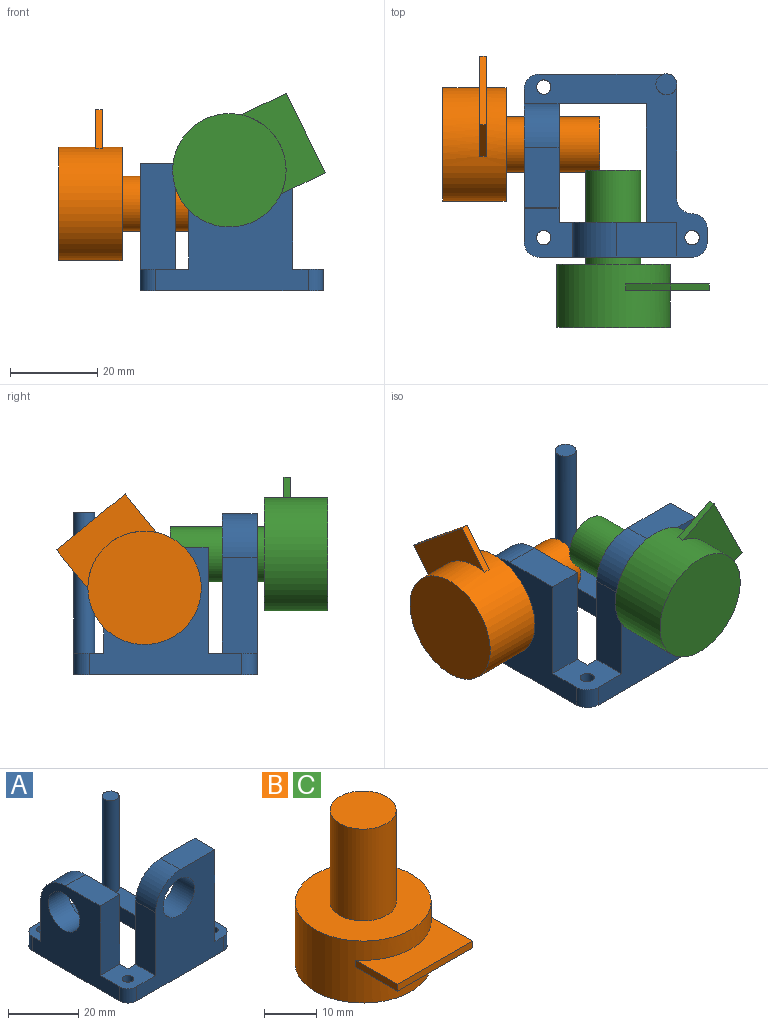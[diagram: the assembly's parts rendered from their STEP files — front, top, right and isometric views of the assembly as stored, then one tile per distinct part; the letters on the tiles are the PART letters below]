
ASSEMBLY  parts=3 mates=2
PART A: 32 faces, bbox 42x42x37.2 mm
  f0: plane 42x42mm, normal (0,0,1), area 458.1mm2, adj f3,f4,f5,f6,f7,f8,f9,f10
  f1: plane 11.25x11.1mm, normal (0,0,1), area 103.6mm2, adj f2,f5,f6,f11,f14,f18,f21,f26
  f2: plane 29.3x27.15mm, normal (1,0,0), area 568.4mm2, adj f1,f3,f11,f12,f20,f21,f22,f28
  f3: plane 20x5mm, normal (0,-1,0), area 100mm2, adj f0,f2,f4,f12
  f4: plane 27.15x5mm, normal (-1,0,0), area 135.7mm2, adj f0,f3,f11,f12
  f5: plane 35x29.3mm, normal (-1,0,0), area 607.6mm2, adj f0,f1,f12,f20,f21,f22,f23,f26
  f6: plane 37x35mm, normal (0,-1,0), area 791.7mm2, adj f0,f1,f12,f17,f18,f19,f24,f26
  f7: plane 5x3mm, normal (1,0,0), area 15mm2, adj f0,f12,f24,f25
  f8: plane 26.1x5mm, normal (1,0,0), area 130.5mm2, adj f0,f9,f12,f27
  f9: cylinder r=2.4mm len=37.2mm, axis (0,0,-1), area 504.4mm2, adj f0,f8,f10,f12,f16
  f10: plane 29.1x5mm, normal (0,1,0), area 145.5mm2, adj f0,f9,f12,f23
  f11: plane 37x27mm, normal (0,1,0), area 716.7mm2, adj f0,f1,f2,f4,f12,f17,f18,f19
  f12: plane 42x42mm, normal (0,0,-1), area 962.2mm2, adj f2,f3,f4,f5,f6,f7,f8,f9
  f13: cylinder r=1.65mm len=5mm, axis (0,0,-1), area 51.8mm2, adj f0,f12
  f14: cylinder r=1.65mm len=5mm, axis (0,0,-1), area 51.8mm2, adj f1,f12
  f15: cylinder r=1.65mm len=5mm, axis (0,0,-1), area 51.8mm2, adj f0,f12
  f16: plane 4.8x4.8mm, normal (0,0,1), area 18.1mm2, adj f9
  f17: plane 32x8mm, normal (1,0,0), area 256mm2, adj f0,f6,f11,f19
  f18: plane 22x8mm, normal (-1,0,0), area 176mm2, adj f1,f6,f11,f31
  f19: plane 13.9x8mm, normal (0,0,1), area 111.2mm2, adj f6,f11,f17,f31
  f20: plane 14.3x8mm, normal (0,1,0), area 114.4mm2, adj f0,f2,f5,f30
  f21: plane 24.3x8mm, normal (0,-1,0), area 194.4mm2, adj f1,f2,f5,f22
  f22: plane 13.9x8mm, normal (0,0,1), area 111.2mm2, adj f2,f5,f21,f30
  f23: cylinder r=3.5mm len=5mm, axis (0,0,1), area 27.5mm2, adj f0,f5,f10,f12
  f24: cylinder r=3.5mm len=5mm, axis (0,0,-1), area 27.5mm2, adj f0,f6,f7,f12
  f25: cylinder r=3.5mm len=5mm, axis (0,0,-1), area 27.5mm2, adj f0,f7,f12,f27
  f26: cylinder r=3.5mm len=5mm, axis (0,0,1), area 27.5mm2, adj f1,f5,f6,f12
  f27: cylinder r=3.5mm len=5mm, axis (0,0,1), area 27.5mm2, adj f0,f8,f12,f25
  f28: cylinder r=6.35mm len=12.7mm, axis (-1,0,0), area 319.2mm2, adj f2,f5
  f29: cylinder r=6.35mm len=12.7mm, axis (0,-1,0), area 319.2mm2, adj f6,f11
  f30: cylinder r=10mm len=10mm, axis (1,0,0), area 125.7mm2, adj f2,f5,f20,f22
  f31: cylinder r=10mm len=10mm, axis (0,1,0), area 125.7mm2, adj f6,f11,f18,f19
PART B: 10 faces, bbox 26x32.5x36 mm
  f0: cylinder r=13mm len=26mm, axis (0,0,1), area 1147.1mm2, adj f1,f3,f4,f5,f6,f9
  f1: plane 11.38x1.6mm, normal (-1,0,0), area 18.2mm2, adj f0,f2,f4,f5
  f2: plane 20.3x1.6mm, normal (0,-1,0), area 32.5mm2, adj f1,f3,f4,f5
  f3: plane 11.38x1.6mm, normal (1,0,0), area 18.2mm2, adj f0,f2,f4,f5
  f4: plane 20.3x11.38mm, normal (0,0,-1), area 162mm2, adj f0,f1,f2,f3
  f5: plane 20.3x11.38mm, normal (0,0,1), area 162mm2, adj f0,f1,f2,f3
  f6: plane 26x26mm, normal (0,0,1), area 405.2mm2, adj f0,f7
  f7: cylinder r=6.33mm len=21.5mm, axis (0,0,-1), area 854.4mm2, adj f6,f8
  f8: plane 12.65x12.65mm, normal (0,0,1), area 125.7mm2, adj f7
  f9: plane 26x26mm, normal (0,0,-1), area 530.9mm2, adj f0
PART C: same geometry as B
PLACE A at identity fixed
PLACE B rot(axis=(-0.67,0.32,-0.67),144.7deg) t=(-29.66,4.8,19.95)mm
PLACE C rot(axis=(-0.75,0.47,0.47),106.2deg) t=(-0.55,-27.13,27.65)mm
MATE cylindrical A.f29 <-> C.f7  axis (0,-1,0) through (-0.55,-21,27.65)mm
MATE cylindrical A.f28 <-> B.f7  axis (-1,0,0) through (-21,4.8,19.95)mm
